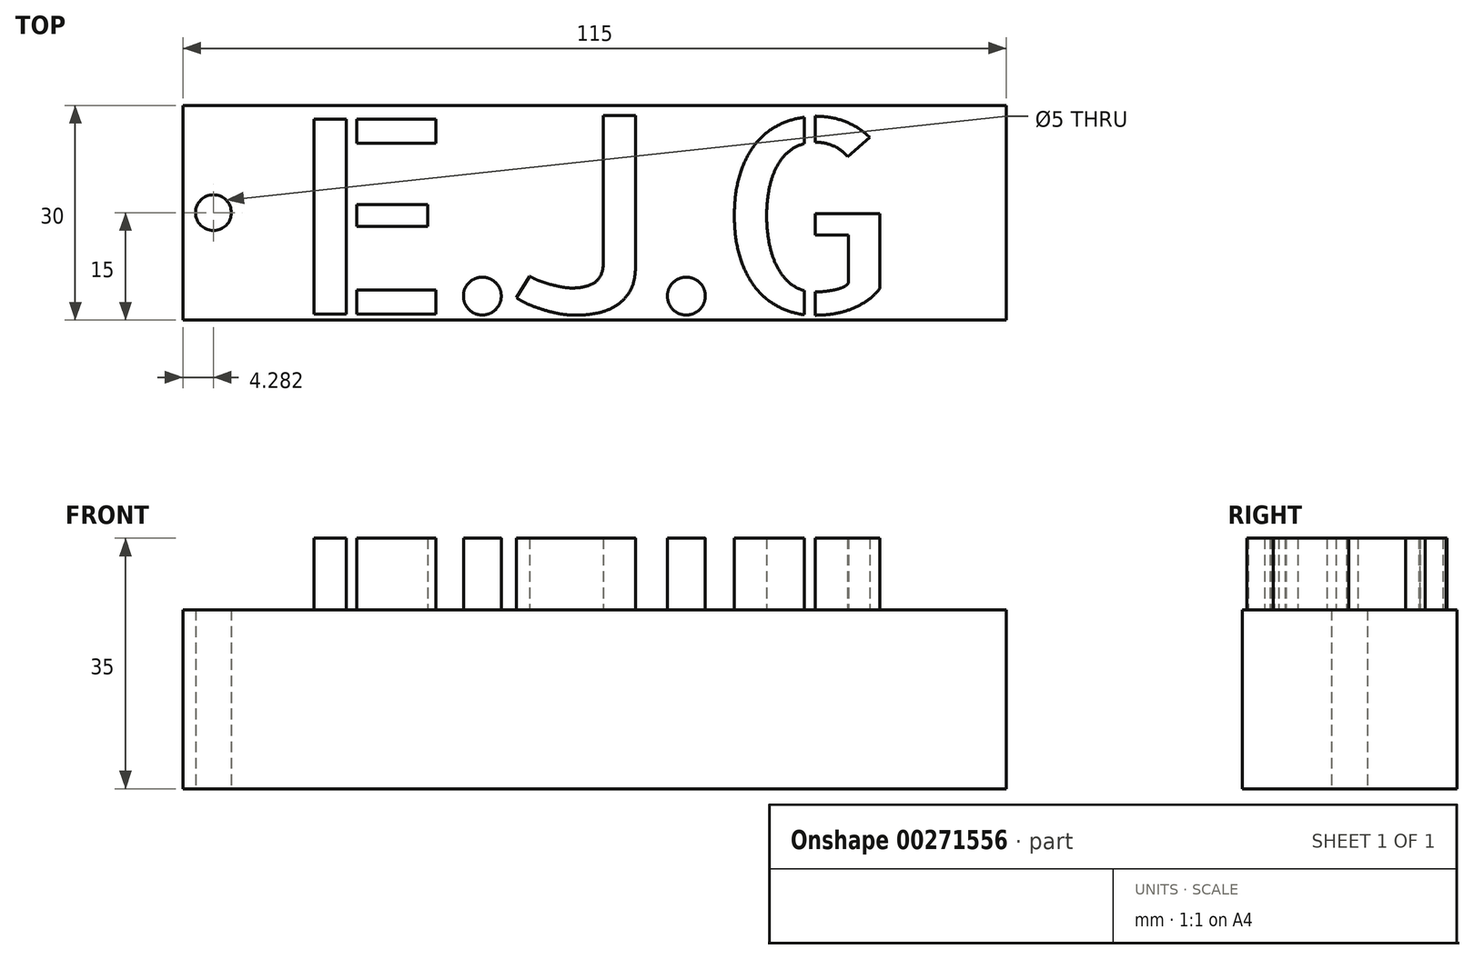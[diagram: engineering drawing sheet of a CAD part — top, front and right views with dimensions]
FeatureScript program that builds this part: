
annotation { "Feature Type Name" : "Feature", "Feature Type Description" : "" }
export const myFeature = defineFeature(function(context is Context, id is Id, definition is map)
    precondition{}
    {
        {
            var Q0;
            Q0=qCreatedBy(makeId("Top.planeOp"),FACE);
            var sketch = newSketch(context, id + "F0", { "sketchPlane" : qUnion([Q0])});
            skLineSegment(sketch, "E0.bottom", {"start": v(-57.5, 15) * mm, "end": v(57.5, 15) * mm});
            skLineSegment(sketch, "E0.top", {"start": v(-57.5, -15) * mm, "end": v(57.5, -15) * mm});
            skLineSegment(sketch, "E0.left", {"start": v(-57.5, 15) * mm, "end": v(-57.5, -15) * mm});
            skLineSegment(sketch, "E0.right", {"start": v(57.5, 15) * mm, "end": v(57.5, -15) * mm});
            skPoint(sketch, "E0.middle", {"position": v(0, 0) * mm});
            skSolve(sketch);
        }
        {
            var Q0;
            Q0=makeQuery(id+"F0.imprint","IMPRINT",FACE,{"disambiguationData":[TD([[makeQuery(id+"F0.imprint","IMPRINT",EDGE,{"derivedFrom":sQuery(id+"F0.wireOp",EDGE,"E0.bottom")}),-1.0]])]});
            extrude(context, id + "F1", {"entities" : qUnion([Q0]), "depth" : 25 * mm});
        }
        {
            var Q0;
            Q0=qCreatedBy(makeId("Top.planeOp"),FACE);
            var sketch = newSketch(context, id + "F2", { "sketchPlane" : qUnion([Q0])});
            skText(sketch, "E1", { "text": "E.J.G", "fontName": "AllertaStencil-Regular.ttf"});
            const initialGuessF2  = {"E1": [-0.0427, -0.01415, 1, 0, 0.0272]};
            skSetInitialGuess(sketch, initialGuessF2);
            skSolve(sketch);
        }
        {
            var Q0;
            Q0 = qSketchRegion(id + "F2", true);
            extrude(context, id + "F3", {"entities" : qUnion([Q0]), "operationType" : NewBodyOperationType.ADD, "depth" : 35 * mm});
        }
        {
            var Q0;
            Q0=qCreatedBy(makeId("Top.planeOp"),FACE);
            var sketch = newSketch(context, id + "F4", { "sketchPlane" : qUnion([Q0])});
            skLineSegment(sketch, "E2", {"start": v(-55.2, 0) * mm, "end": v(-53.22, 0) * mm});
            skLineSegment(sketch, "E3", {"start": v(-53.22, 0) * mm, "end": v(-51.15, 0) * mm});
            skLineSegment(sketch, "E4", {"start": v(-53.37, 2) * mm, "end": v(-53.22, 0) * mm});
            skSolve(sketch);
        }
        {
            var Q0;
            Q0=sQuery(id+"F4.wireOp",VERTEX,"E3.start");
            var Q1;
            Q1=makeQuery(id+"F1.opExtrude","SWEPT_BODY",BODY,{"disambiguationData":[OSD([sQuery(id+"F0.wireOp",EDGE,"E0.bottom"),sQuery(id+"F0.wireOp",EDGE,"E0.top"),sQuery(id+"F0.wireOp",EDGE,"E0.left"),sQuery(id+"F0.wireOp",EDGE,"E0.right")])]});
            hole(context, id + "F5", {"style" : HoleStyle.SIMPLE, "endStyle" : HoleEndStyle.THROUGH, "oppositeDirection" : true, "holeDiameter" : 5 * mm, "tappedDepth" : 12 * mm, "tapClearance" : 3, "locations" : qUnion([Q0]), "scope" : qUnion([Q1])});
        }
    });
